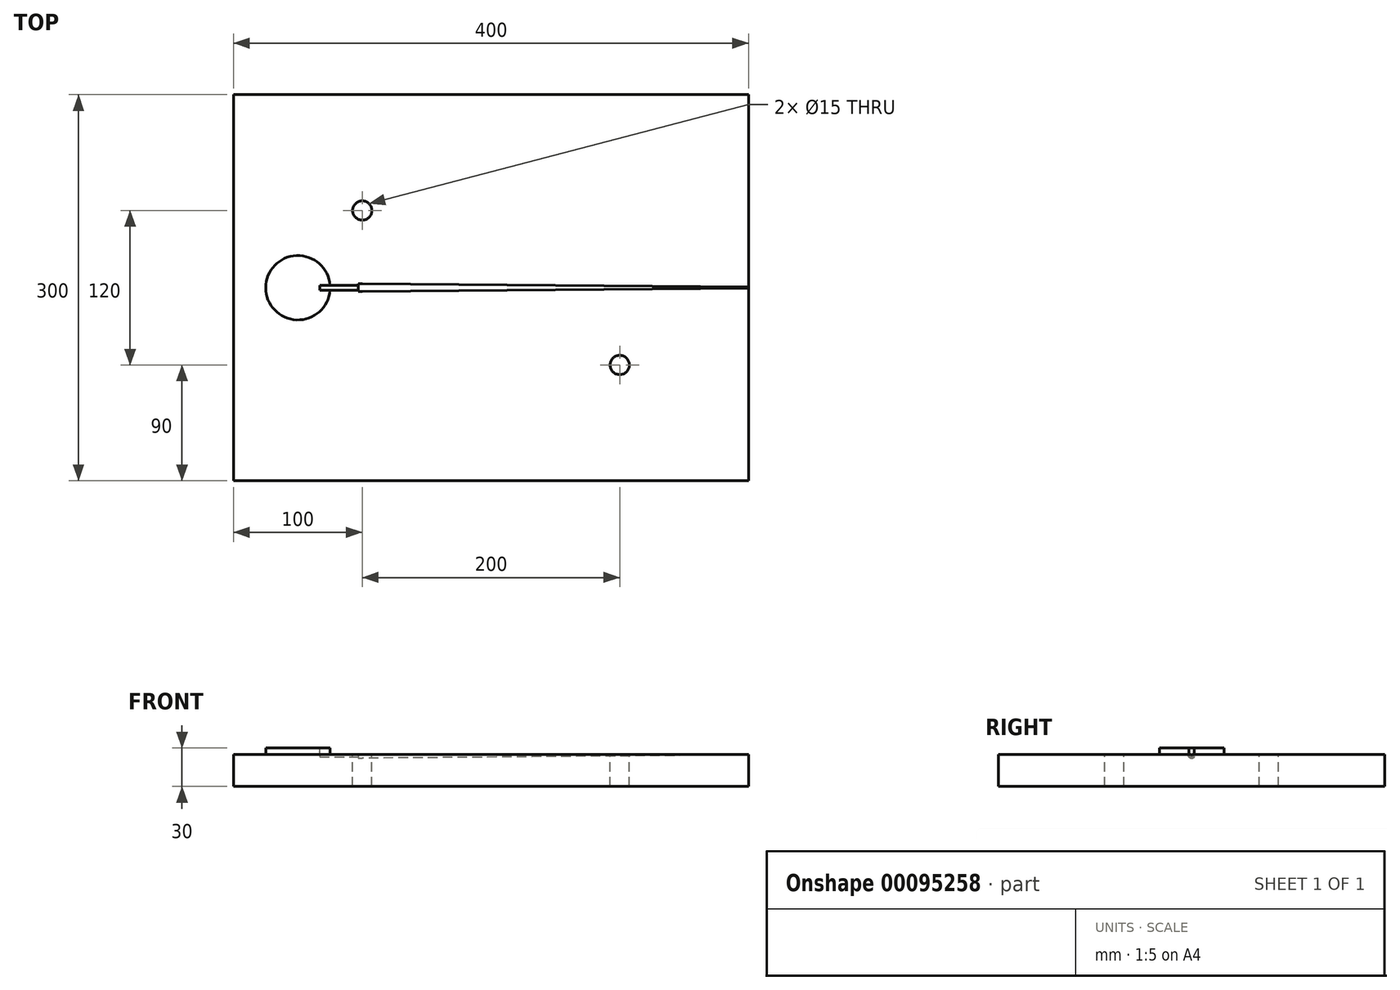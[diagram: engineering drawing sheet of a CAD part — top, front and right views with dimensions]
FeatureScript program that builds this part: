
annotation { "Feature Type Name" : "Feature", "Feature Type Description" : "" }
export const myFeature = defineFeature(function(context is Context, id is Id, definition is map)
    precondition{}
    {
        {
            var Q0;
            Q0=qCreatedBy(makeId("Top.planeOp"),FACE);
            var sketch = newSketch(context, id + "F0", { "sketchPlane" : qUnion([Q0])});
            skLineSegment(sketch, "E0.bottom", {"start": v(200, 150) * mm, "end": v(-200, 150) * mm});
            skLineSegment(sketch, "E0.top", {"start": v(200, -150) * mm, "end": v(-200, -150) * mm});
            skLineSegment(sketch, "E0.left", {"start": v(200, 150) * mm, "end": v(200, -150) * mm});
            skLineSegment(sketch, "E0.right", {"start": v(-200, 150) * mm, "end": v(-200, -150) * mm});
            skPoint(sketch, "E0.middle", {"position": v(0, 0) * mm});
            skSolve(sketch);
        }
        {
            var Q0;
            Q0=qSketchRegion(id+"F0",true);
            extrude(context, id + "F1", {"entities" : qUnion([Q0]), "depth" : 25 * mm});
        }
        {
            var Q0;
            Q0=makeQuery(id+"F1.opExtrude","CAP_FACE",FACE,{"disambiguationData":[OSD([sQuery(id+"F0.wireOp",EDGE,"E0.bottom"),sQuery(id+"F0.wireOp",EDGE,"E0.top"),sQuery(id+"F0.wireOp",EDGE,"E0.left"),sQuery(id+"F0.wireOp",EDGE,"E0.right")])],"isStart":false});
            var sketch = newSketch(context, id + "F2", { "sketchPlane" : qUnion([Q0])});
            skLineSegment(sketch, "E1", {"start": v(200, 0.5) * mm, "end": v(-100, 3) * mm});
            skLineSegment(sketch, "E2", {"start": v(-100, 3) * mm, "end": v(-100, 0) * mm});
            skLineSegment(sketch, "E3", {"start": v(-100, 0) * mm, "end": v(200, 0) * mm});
            skLineSegment(sketch, "E4", {"start": v(200, 0.5) * mm, "end": v(200, 0) * mm});
            skSolve(sketch);
        }
        {
            var Q0;
            Q0=qSketchRegion(id+"F2",true);
            var Q1;
            Q1=sQuery(id+"F2.wireOp",EDGE,"E3");
            revolve(context, id + "F3", {"operationType" : NewBodyOperationType.REMOVE, "entities" : qUnion([Q0]), "axis" : qUnion([Q1]), "revolveType" : RevolveType.FULL, "oppositeDirection" : true});
        }
        {
            var Q0;
            {var subQ0=sQuery(id+"F0.wireOp",EDGE,"E0.right");var subQ1=sQuery(id+"F0.wireOp",EDGE,"E0.left");var subQ2=sQuery(id+"F0.wireOp",EDGE,"E0.top");var subQ3=sQuery(id+"F0.wireOp",EDGE,"E0.bottom");Q0=makeQuery(id+"F6EEDHxu7RHCoKd_1.boolean.opBoolean","SPLIT",FACE,{"disambiguationData":[TD([makeQuery(id+"F1.opExtrude","SWEPT_FACE",FACE,{"disambiguationData":[OSD([subQ3])]})])],"derivedFrom":makeQuery(id+"F1.opExtrude","CAP_FACE",FACE,{"disambiguationData":[OSD([subQ3,subQ2,subQ1,subQ0])],"isStart":false})});}
            var sketch = newSketch(context, id + "F4", { "sketchPlane" : qUnion([Q0])});
            skCircle(sketch, "E5", {"center": v(-150, 0) * mm, "radius": 25 * mm});
            skSolve(sketch);
        }
        {
            var Q0;
            Q0=qSketchRegion(id+"F4",true);
            extrude(context, id + "F5", {"entities" : qUnion([Q0]), "operationType" : NewBodyOperationType.ADD, "depth" : 5 * mm});
        }
        {
            var Q0;
            Q0=makeQuery(id+"F3.boolean.opBoolean","COPY",FACE,{"derivedFrom":makeQuery(id+"F3.opRevolve","SWEPT_FACE",FACE,{"disambiguationData":[OSD([sQuery(id+"F2.wireOp",EDGE,"E2")])]})});
            var sketch = newSketch(context, id + "F6", { "sketchPlane" : qUnion([Q0])});
            skCircle(sketch, "E6", {"center": v(0, 25) * mm, "radius": 3 * mm});
            skSolve(sketch);
        }
        {
            var Q0;
            Q0=qSketchRegion(id+"F6",true);
            extrude(context, id + "F7", {"entities" : qUnion([Q0]), "operationType" : NewBodyOperationType.REMOVE, "oppositeDirection" : true, "depth" : 3 * mm});
        }
        {
            var Q0;
            Q0=makeQuery(id+"F7.boolean.opBoolean","COPY",FACE,{"derivedFrom":makeQuery(id+"F7.opExtrude","CAP_FACE",FACE,{"disambiguationData":[OSD([sQuery(id+"F6.wireOp",EDGE,"E6")])],"isStart":false})});
            var sketch = newSketch(context, id + "F8", { "sketchPlane" : qUnion([Q0])});
            skCircle(sketch, "E7", {"center": v(0, 25) * mm, "radius": 2 * mm});
            skSolve(sketch);
        }
        {
            var Q0;
            Q0=qSketchRegion(id+"F8",true);
            var Q1;
            Q1=makeQuery(id+"F5.opExtrude","SWEPT_FACE",FACE,{"disambiguationData":[OSD([sQuery(id+"F4.wireOp",EDGE,"E5")])]});
            extrude(context, id + "F9", {"entities" : qUnion([Q0]), "operationType" : NewBodyOperationType.REMOVE, "endBound" : BoundingType.UP_TO_SURFACE, "oppositeDirection" : true, "endBoundEntityFace" : qUnion([Q1]), "depth" : 25 * mm});
        }
        {
            var Q0;
            Q0=makeQuery(id+"F5.opExtrude","CAP_FACE",FACE,{"disambiguationData":[OSD([sQuery(id+"F4.wireOp",EDGE,"E5")])],"isStart":false});
            var sketch = newSketch(context, id + "F10", { "sketchPlane" : qUnion([Q0])});
            skLineSegment(sketch, "E8.bottom", {"start": v(-122, 2) * mm, "end": v(-133, 2) * mm});
            skLineSegment(sketch, "E8.top", {"start": v(-122, -2) * mm, "end": v(-133, -2) * mm});
            skLineSegment(sketch, "E8.left", {"start": v(-122, 2) * mm, "end": v(-122, -2) * mm});
            skLineSegment(sketch, "E8.right", {"start": v(-133, 2) * mm, "end": v(-133, -2) * mm});
            skSolve(sketch);
        }
        {
            var Q0;
            Q0 = qSketchRegion(id + "F10", true);
            extrude(context, id + "F11", {"entities" : qUnion([Q0]), "operationType" : NewBodyOperationType.REMOVE, "oppositeDirection" : true, "depth" : 5 * mm});
        }
        {
            var Q0;
            Q0=makeQuery(id+"F11.boolean.opBoolean","COPY",FACE,{"derivedFrom":makeQuery(id+"F11.opExtrude","CAP_FACE",FACE,{"disambiguationData":[OSD([sQuery(id+"F10.wireOp",EDGE,"E8.bottom"),sQuery(id+"F10.wireOp",EDGE,"E8.top"),sQuery(id+"F10.wireOp",EDGE,"E8.left"),sQuery(id+"F10.wireOp",EDGE,"E8.right")])],"isStart":false})});
            var sketch = newSketch(context, id + "F12", { "sketchPlane" : qUnion([Q0])});
            skLineSegment(sketch, "E9", {"start": v(-133, -2) * mm, "end": v(-123.64, -2) * mm});
            skLineSegment(sketch, "E10", {"start": v(-133, -2) * mm, "end": v(-133, 2) * mm});
            skLineSegment(sketch, "E11", {"start": v(-133, 2) * mm, "end": v(-123.64, 2) * mm});
            skLineSegment(sketch, "E12", {"start": v(-123.64, 2) * mm, "end": v(-123.64, -2) * mm});
            skLineSegment(sketch, "E13", {"start": v(-133, 0) * mm, "end": v(-123.64, 0) * mm});
            skSolve(sketch);
        }
        {
            var Q0;
            {var subQ0=sQuery(id+"F12.wireOp",EDGE,"E11");var subQ1=sQuery(id+"F12.wireOp",EDGE,"E10");var subQ2=makeQuery(id+"F12.imprint","INTERSECT",VERTEX,{"derivedFrom":[subQ1,subQ0]});Q0=makeQuery(id+"F12.imprint","IMPRINT",FACE,{"disambiguationData":[TD([[makeQuery(id+"F12.imprint","IMPRINT",EDGE,{"disambiguationData":[TD([[subQ2,-1.0]])],"derivedFrom":subQ1}),1.0]])]});}
            var Q1;
            {var subQ0=sQuery(id+"F12.wireOp",EDGE,"E11");var subQ4=sQuery(id+"F12.wireOp",EDGE,"E12");var subQ5=makeQuery(id+"F12.imprint","INTERSECT",VERTEX,{"derivedFrom":[subQ0,subQ4]});Q1=makeQuery(id+"F12.imprint","IMPRINT",FACE,{"disambiguationData":[TD([[makeQuery(id+"F12.imprint","IMPRINT",EDGE,{"disambiguationData":[TD([[subQ5,-1.0]])],"derivedFrom":subQ4}),-1.0]])]});}
            var Q2;
            Q2=sQuery(id+"F12.wireOp",EDGE,"E13");
            revolve(context, id + "F13", {"operationType" : NewBodyOperationType.REMOVE, "entities" : qUnion([Q0, Q1]), "axis" : qUnion([Q2]), "revolveType" : RevolveType.FULL, "oppositeDirection" : true});
        }
        {
            var Q0;
            Q0=makeQuery(id+"F1.opExtrude","CAP_FACE",FACE,{"disambiguationData":[OSD([sQuery(id+"F0.wireOp",EDGE,"E0.bottom"),sQuery(id+"F0.wireOp",EDGE,"E0.top"),sQuery(id+"F0.wireOp",EDGE,"E0.left"),sQuery(id+"F0.wireOp",EDGE,"E0.right")])],"isStart":false});
            var sketch = newSketch(context, id + "F14", { "sketchPlane" : qUnion([Q0])});
            skCircle(sketch, "E14", {"center": v(100, -60) * mm, "radius": 7.5 * mm});
            skCircle(sketch, "E15", {"center": v(-100, 60) * mm, "radius": 7.5 * mm});
            skSolve(sketch);
        }
        {
            var Q0;
            Q0 = qSketchRegion(id + "F14", true);
            extrude(context, id + "F15", {"entities" : qUnion([Q0]), "operationType" : NewBodyOperationType.REMOVE, "endBound" : BoundingType.THROUGH_ALL, "oppositeDirection" : true, "depth" : 25 * mm});
        }
    });
